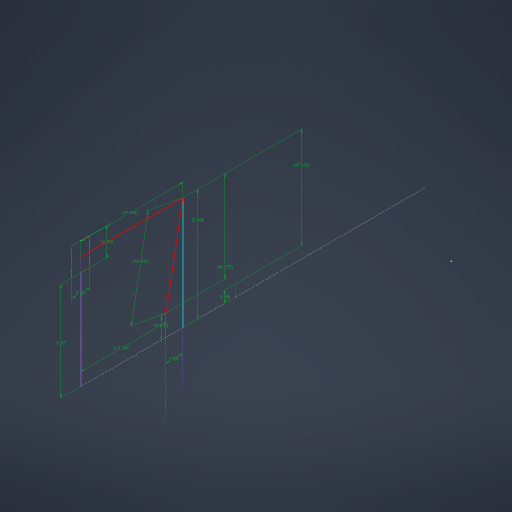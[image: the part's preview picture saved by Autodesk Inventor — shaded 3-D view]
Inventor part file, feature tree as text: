
AUTODESK INVENTOR PART (.ipt)
format: ipt  version: 2023 (Build 270158000, 158)  size: 181,760 bytes
history: native  units: in
note: dims shown in document units (in); Inventor stores cm internally (conversion verified against a paired STEP export)
features: sketch x1
ambient origin geometry x8: Origin, YZ Plane, XZ Plane, XY Plane, X Axis, Y Axis, Z Axis, Center Point
feature tree (1):
  sketch  "Sketch1"  dims[d0=46.0in d1=12.9921in d2=8.375in d3=39.75in d4=7.905in d5=43.403in d6=52.4961in d7=9.819in d8=42.677in d9=47.655in d10=5.36in d11=47.1361in]
